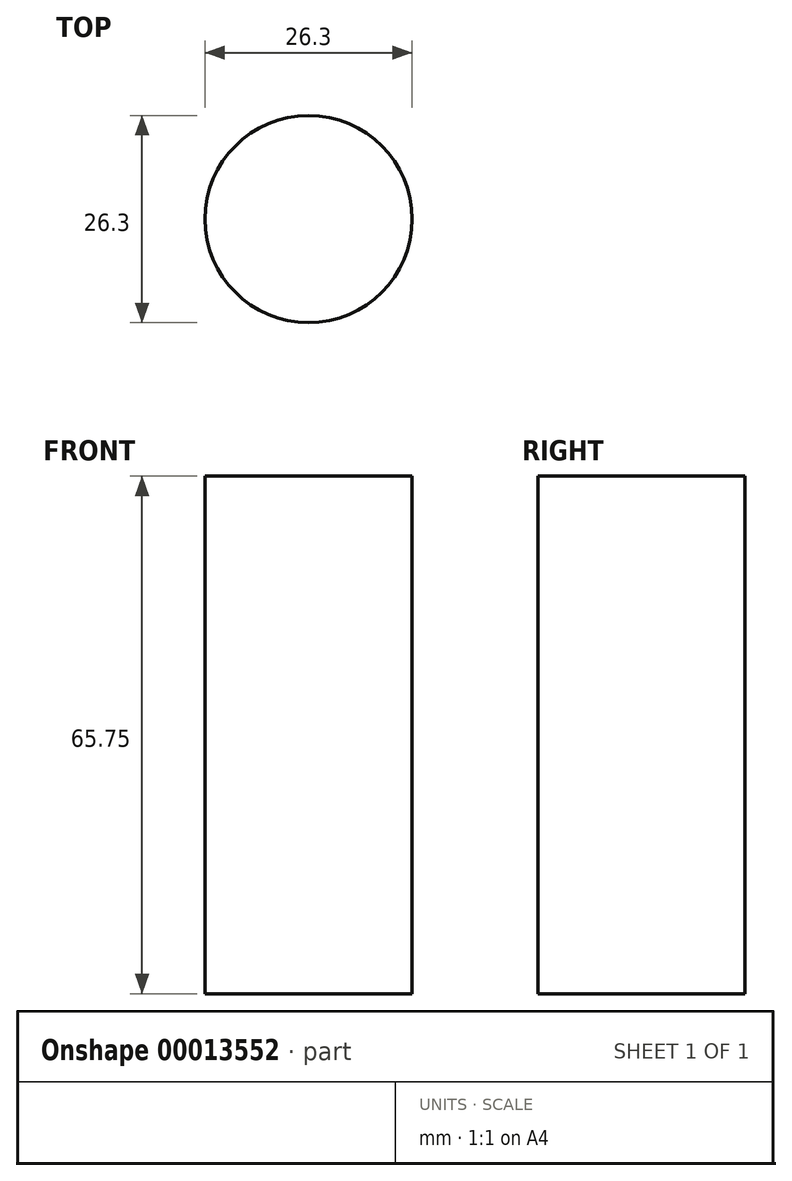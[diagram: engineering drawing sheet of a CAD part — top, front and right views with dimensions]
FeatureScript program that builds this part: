
annotation { "Feature Type Name" : "Feature", "Feature Type Description" : "" }
export const myFeature = defineFeature(function(context is Context, id is Id, definition is map)
    precondition{}
    {
        {
            var Q0;
            Q0=qCreatedBy(makeId("Top.planeOp"),FACE);
            var sketch = newSketch(context, id + "F0", { "sketchPlane" : qUnion([Q0])});
            skCircle(sketch, "E0", {"center": v(0, 0) * mm, "radius": 13.15 * mm});
            skSolve(sketch);
        }
        {
            var Q0;
            Q0 = qSketchRegion(id + "F0", true);
            extrude(context, id + "F1", {"entities" : qUnion([Q0]), "depth" : 65.75 * mm});
        }
    });
